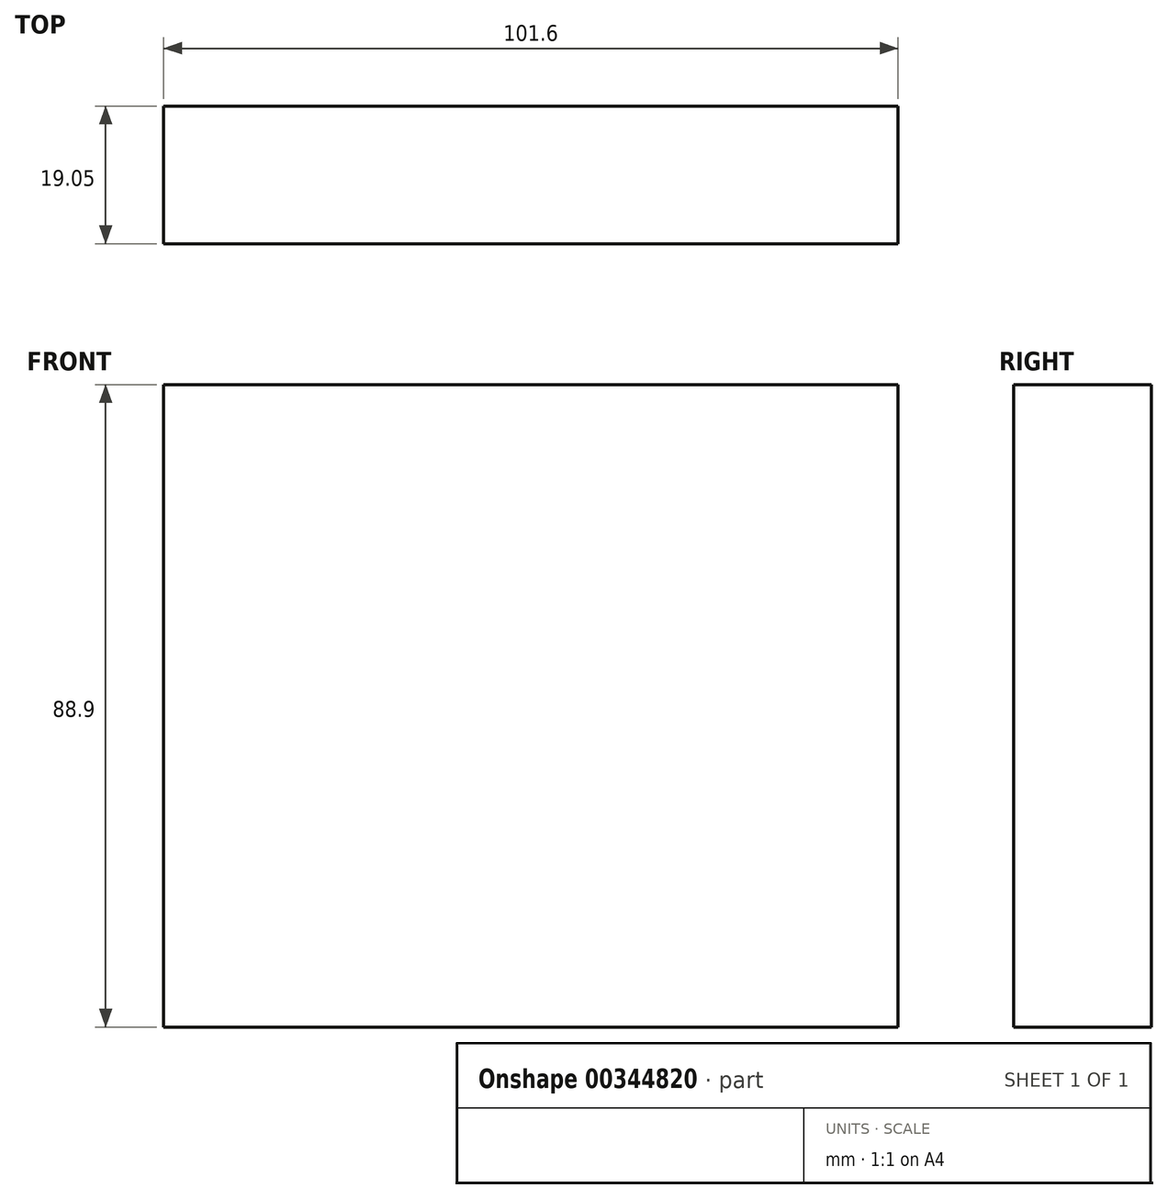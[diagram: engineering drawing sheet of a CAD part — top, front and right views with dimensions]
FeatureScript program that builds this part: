
annotation { "Feature Type Name" : "Feature", "Feature Type Description" : "" }
export const myFeature = defineFeature(function(context is Context, id is Id, definition is map)
    precondition{}
    {
        {
            var Q0;
            Q0=qCreatedBy(makeId("Front.planeOp"),FACE);
            var sketch = newSketch(context, id + "F0", { "sketchPlane" : qUnion([Q0])});
            skLineSegment(sketch, "E0.bottom", {"start": v(0, 0) * mm, "end": v(101.6, 0) * mm});
            skLineSegment(sketch, "E0.top", {"start": v(0, 88.9) * mm, "end": v(101.6, 88.9) * mm});
            skLineSegment(sketch, "E0.left", {"start": v(0, 0) * mm, "end": v(0, 88.9) * mm});
            skLineSegment(sketch, "E0.right", {"start": v(101.6, 0) * mm, "end": v(101.6, 88.9) * mm});
            skSolve(sketch);
        }
        {
            var Q0;
            Q0=makeQuery(id+"F0.imprint","IMPRINT",FACE,{"disambiguationData":[TD([[makeQuery(id+"F0.imprint","IMPRINT",EDGE,{"derivedFrom":sQuery(id+"F0.wireOp",EDGE,"E0.bottom")}),1.0]])]});
            extrude(context, id + "F1", {"entities" : qUnion([Q0]), "depth" : 19.05 * mm});
        }
    });
